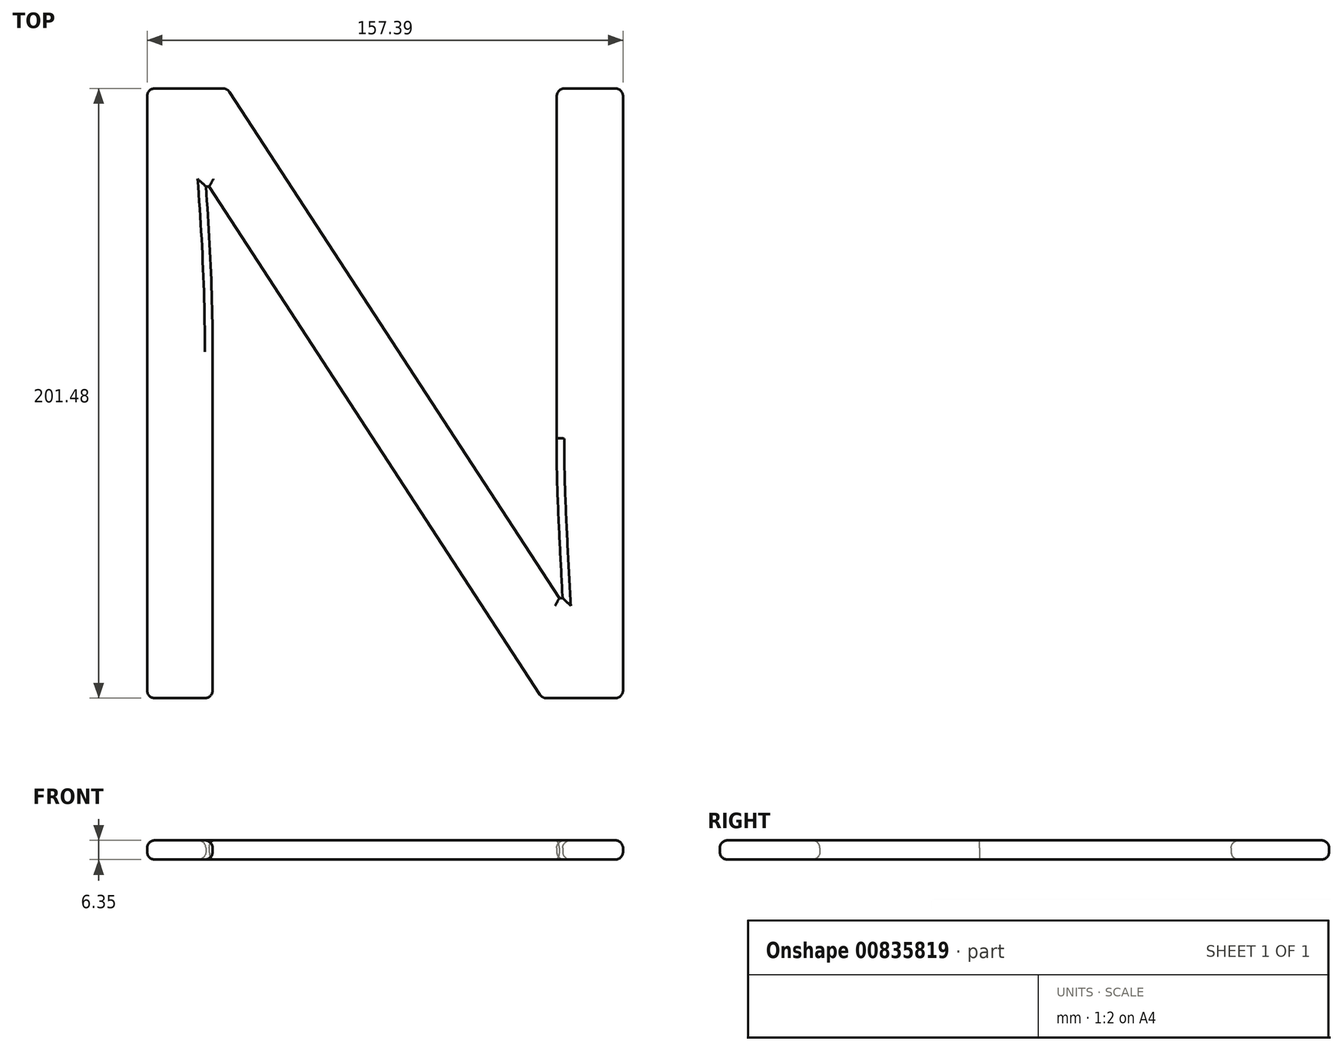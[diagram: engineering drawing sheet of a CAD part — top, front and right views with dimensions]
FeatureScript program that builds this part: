
annotation { "Feature Type Name" : "Feature", "Feature Type Description" : "" }
export const myFeature = defineFeature(function(context is Context, id is Id, definition is map)
    precondition{}
    {
        {
            var Q0;
            Q0=qCreatedBy(makeId("Top.planeOp"),FACE);
            var sketch = newSketch(context, id + "F0", { "sketchPlane" : qUnion([Q0])});
            skText(sketch, "E0", { "text": "N", "fontName": "OpenSans-Regular.ttf"});
            const initialGuessF0  = {"E0": [0.01101, 0, 1, 0, 0.2032]};
            skSetInitialGuess(sketch, initialGuessF0);
            skSolve(sketch);
        }
        {
            var Q0;
            Q0=makeQuery(id+"F0.imprint","IMPRINT",FACE,{"disambiguationData":[TD([[makeQuery(id+"F0.imprint","IMPRINT",EDGE,{"derivedFrom":sQuery(id+"F0.wireOp",EDGE,"E0.sketch_text.stroke-0")}),-1.0]])]});
            extrude(context, id + "F1", {"entities" : qUnion([Q0]), "depth" : 6.35 * mm, "offsetDistance" : 25.4 * mm});
        }
        {
            var Q0;
            Q0=makeQuery(id+"F1.opExtrude","CAP_FACE",FACE,{"disambiguationData":[OSD([sQuery(id+"F0.wireOp",EDGE,"E0.sketch_text.stroke-0"),sQuery(id+"F0.wireOp",EDGE,"E0.sketch_text.stroke-1"),sQuery(id+"F0.wireOp",EDGE,"E0.sketch_text.stroke-2"),sQuery(id+"F0.wireOp",EDGE,"E0.sketch_text.stroke-3"),sQuery(id+"F0.wireOp",EDGE,"E0.sketch_text.stroke-4"),sQuery(id+"F0.wireOp",EDGE,"E0.sketch_text.stroke-5"),sQuery(id+"F0.wireOp",EDGE,"E0.sketch_text.stroke-6"),sQuery(id+"F0.wireOp",EDGE,"E0.sketch_text.stroke-7"),sQuery(id+"F0.wireOp",EDGE,"E0.sketch_text.stroke-8"),sQuery(id+"F0.wireOp",EDGE,"E0.sketch_text.stroke-9"),sQuery(id+"F0.wireOp",EDGE,"E0.sketch_text.stroke-10"),sQuery(id+"F0.wireOp",EDGE,"E0.sketch_text.stroke-11"),sQuery(id+"F0.wireOp",EDGE,"E0.sketch_text.stroke-12"),sQuery(id+"F0.wireOp",EDGE,"E0.sketch_text.stroke-13"),sQuery(id+"F0.wireOp",EDGE,"E0.sketch_text.stroke-14")])],"isStart":true});
            var Q1;
            Q1=makeQuery(id+"F1.opExtrude","CAP_FACE",FACE,{"disambiguationData":[OSD([sQuery(id+"F0.wireOp",EDGE,"E0.sketch_text.stroke-0"),sQuery(id+"F0.wireOp",EDGE,"E0.sketch_text.stroke-1"),sQuery(id+"F0.wireOp",EDGE,"E0.sketch_text.stroke-2"),sQuery(id+"F0.wireOp",EDGE,"E0.sketch_text.stroke-3"),sQuery(id+"F0.wireOp",EDGE,"E0.sketch_text.stroke-4"),sQuery(id+"F0.wireOp",EDGE,"E0.sketch_text.stroke-5"),sQuery(id+"F0.wireOp",EDGE,"E0.sketch_text.stroke-6"),sQuery(id+"F0.wireOp",EDGE,"E0.sketch_text.stroke-7"),sQuery(id+"F0.wireOp",EDGE,"E0.sketch_text.stroke-8"),sQuery(id+"F0.wireOp",EDGE,"E0.sketch_text.stroke-9"),sQuery(id+"F0.wireOp",EDGE,"E0.sketch_text.stroke-10"),sQuery(id+"F0.wireOp",EDGE,"E0.sketch_text.stroke-11"),sQuery(id+"F0.wireOp",EDGE,"E0.sketch_text.stroke-12"),sQuery(id+"F0.wireOp",EDGE,"E0.sketch_text.stroke-13"),sQuery(id+"F0.wireOp",EDGE,"E0.sketch_text.stroke-14")])],"isStart":false});
            fillet(context, id + "F2", {"entities" : qUnion([Q0, Q1]), "radius" : 2.54 * mm, "tangentPropagation" : true, "allowEdgeOverflow" : false});
        }
        {
            var Q0;
            Q0=makeQuery(id+"F2.opFillet","BLEND_EDGE",EDGE,{"blendedFrom":[makeQuery(id+"F1.opExtrude","CAP_EDGE",EDGE,{"disambiguationData":[OSD([sQuery(id+"F0.wireOp",EDGE,"E0.sketch_text.stroke-5")])],"isStart":false}),makeQuery(id+"F1.opExtrude","CAP_EDGE",EDGE,{"disambiguationData":[OSD([sQuery(id+"F0.wireOp",EDGE,"E0.sketch_text.stroke-6")])],"isStart":false})],"blendedInto":[]});
            var Q1;
            Q1=makeQuery(id+"F1.opExtrude","SWEPT_EDGE",EDGE,{"disambiguationData":[OSD([sQuery(id+"F0.wireOp",EDGE,"E0.sketch_text.stroke-5"),sQuery(id+"F0.wireOp",EDGE,"E0.sketch_text.stroke-6")])]});
            var Q2;
            Q2=makeQuery(id+"F2.opFillet","BLEND_EDGE",EDGE,{"blendedFrom":[makeQuery(id+"F1.opExtrude","CAP_EDGE",EDGE,{"disambiguationData":[OSD([sQuery(id+"F0.wireOp",EDGE,"E0.sketch_text.stroke-5")])],"isStart":true}),makeQuery(id+"F1.opExtrude","CAP_EDGE",EDGE,{"disambiguationData":[OSD([sQuery(id+"F0.wireOp",EDGE,"E0.sketch_text.stroke-6")])],"isStart":true})],"blendedInto":[]});
            var Q3;
            Q3=makeQuery(id+"F2.opFillet","BLEND_EDGE",EDGE,{"blendedFrom":[makeQuery(id+"F1.opExtrude","CAP_EDGE",EDGE,{"disambiguationData":[OSD([sQuery(id+"F0.wireOp",EDGE,"E0.sketch_text.stroke-4")])],"isStart":true}),makeQuery(id+"F1.opExtrude","CAP_EDGE",EDGE,{"disambiguationData":[OSD([sQuery(id+"F0.wireOp",EDGE,"E0.sketch_text.stroke-5")])],"isStart":true})],"blendedInto":[]});
            var Q4;
            Q4=makeQuery(id+"F1.opExtrude","SWEPT_EDGE",EDGE,{"disambiguationData":[OSD([sQuery(id+"F0.wireOp",EDGE,"E0.sketch_text.stroke-4"),sQuery(id+"F0.wireOp",EDGE,"E0.sketch_text.stroke-5")])]});
            var Q5;
            Q5=makeQuery(id+"F2.opFillet","BLEND_EDGE",EDGE,{"blendedFrom":[makeQuery(id+"F1.opExtrude","CAP_EDGE",EDGE,{"disambiguationData":[OSD([sQuery(id+"F0.wireOp",EDGE,"E0.sketch_text.stroke-4")])],"isStart":false}),makeQuery(id+"F1.opExtrude","CAP_EDGE",EDGE,{"disambiguationData":[OSD([sQuery(id+"F0.wireOp",EDGE,"E0.sketch_text.stroke-5")])],"isStart":false})],"blendedInto":[]});
            var Q6;
            Q6=makeQuery(id+"F2.opFillet","BLEND_EDGE",EDGE,{"blendedFrom":[makeQuery(id+"F1.opExtrude","CAP_EDGE",EDGE,{"disambiguationData":[OSD([sQuery(id+"F0.wireOp",EDGE,"E0.sketch_text.stroke-6")])],"isStart":false}),makeQuery(id+"F1.opExtrude","CAP_EDGE",EDGE,{"disambiguationData":[OSD([sQuery(id+"F0.wireOp",EDGE,"E0.sketch_text.stroke-7")])],"isStart":false})],"blendedInto":[]});
            var Q7;
            Q7=makeQuery(id+"F2.opFillet","BLEND_EDGE",EDGE,{"blendedFrom":[makeQuery(id+"F1.opExtrude","CAP_EDGE",EDGE,{"disambiguationData":[OSD([sQuery(id+"F0.wireOp",EDGE,"E0.sketch_text.stroke-7")])],"isStart":false}),makeQuery(id+"F1.opExtrude","CAP_EDGE",EDGE,{"disambiguationData":[OSD([sQuery(id+"F0.wireOp",EDGE,"E0.sketch_text.stroke-8")])],"isStart":false})],"blendedInto":[]});
            var Q8;
            Q8=makeQuery(id+"F2.opFillet","BLEND_EDGE",EDGE,{"blendedFrom":[makeQuery(id+"F1.opExtrude","CAP_EDGE",EDGE,{"disambiguationData":[OSD([sQuery(id+"F0.wireOp",EDGE,"E0.sketch_text.stroke-0")])],"isStart":false}),makeQuery(id+"F1.opExtrude","CAP_EDGE",EDGE,{"disambiguationData":[OSD([sQuery(id+"F0.wireOp",EDGE,"E0.sketch_text.stroke-1")])],"isStart":false})],"blendedInto":[]});
            var Q9;
            Q9=makeQuery(id+"F2.opFillet","BLEND_EDGE",EDGE,{"blendedFrom":[makeQuery(id+"F1.opExtrude","CAP_EDGE",EDGE,{"disambiguationData":[OSD([sQuery(id+"F0.wireOp",EDGE,"E0.sketch_text.stroke-0")])],"isStart":false}),makeQuery(id+"F1.opExtrude","CAP_EDGE",EDGE,{"disambiguationData":[OSD([sQuery(id+"F0.wireOp",EDGE,"E0.sketch_text.stroke-14")])],"isStart":false})],"blendedInto":[]});
            var Q10;
            Q10=makeQuery(id+"F2.opFillet","BLEND_EDGE",EDGE,{"blendedFrom":[makeQuery(id+"F1.opExtrude","CAP_EDGE",EDGE,{"disambiguationData":[OSD([sQuery(id+"F0.wireOp",EDGE,"E0.sketch_text.stroke-12")])],"isStart":false}),makeQuery(id+"F1.opExtrude","CAP_EDGE",EDGE,{"disambiguationData":[OSD([sQuery(id+"F0.wireOp",EDGE,"E0.sketch_text.stroke-13")])],"isStart":false})],"blendedInto":[]});
            var Q11;
            Q11=makeQuery(id+"F2.opFillet","BLEND_EDGE",EDGE,{"blendedFrom":[makeQuery(id+"F1.opExtrude","CAP_EDGE",EDGE,{"disambiguationData":[OSD([sQuery(id+"F0.wireOp",EDGE,"E0.sketch_text.stroke-13")])],"isStart":false}),makeQuery(id+"F1.opExtrude","CAP_EDGE",EDGE,{"disambiguationData":[OSD([sQuery(id+"F0.wireOp",EDGE,"E0.sketch_text.stroke-14")])],"isStart":false})],"blendedInto":[]});
            fillet(context, id + "F3", {"entities" : qUnion([Q0, Q1, Q2, Q3, Q4, Q5, Q6, Q7, Q8, Q9, Q10, Q11]), "radius" : 2.54 * mm, "tangentPropagation" : true, "allowEdgeOverflow" : false});
        }
    });
